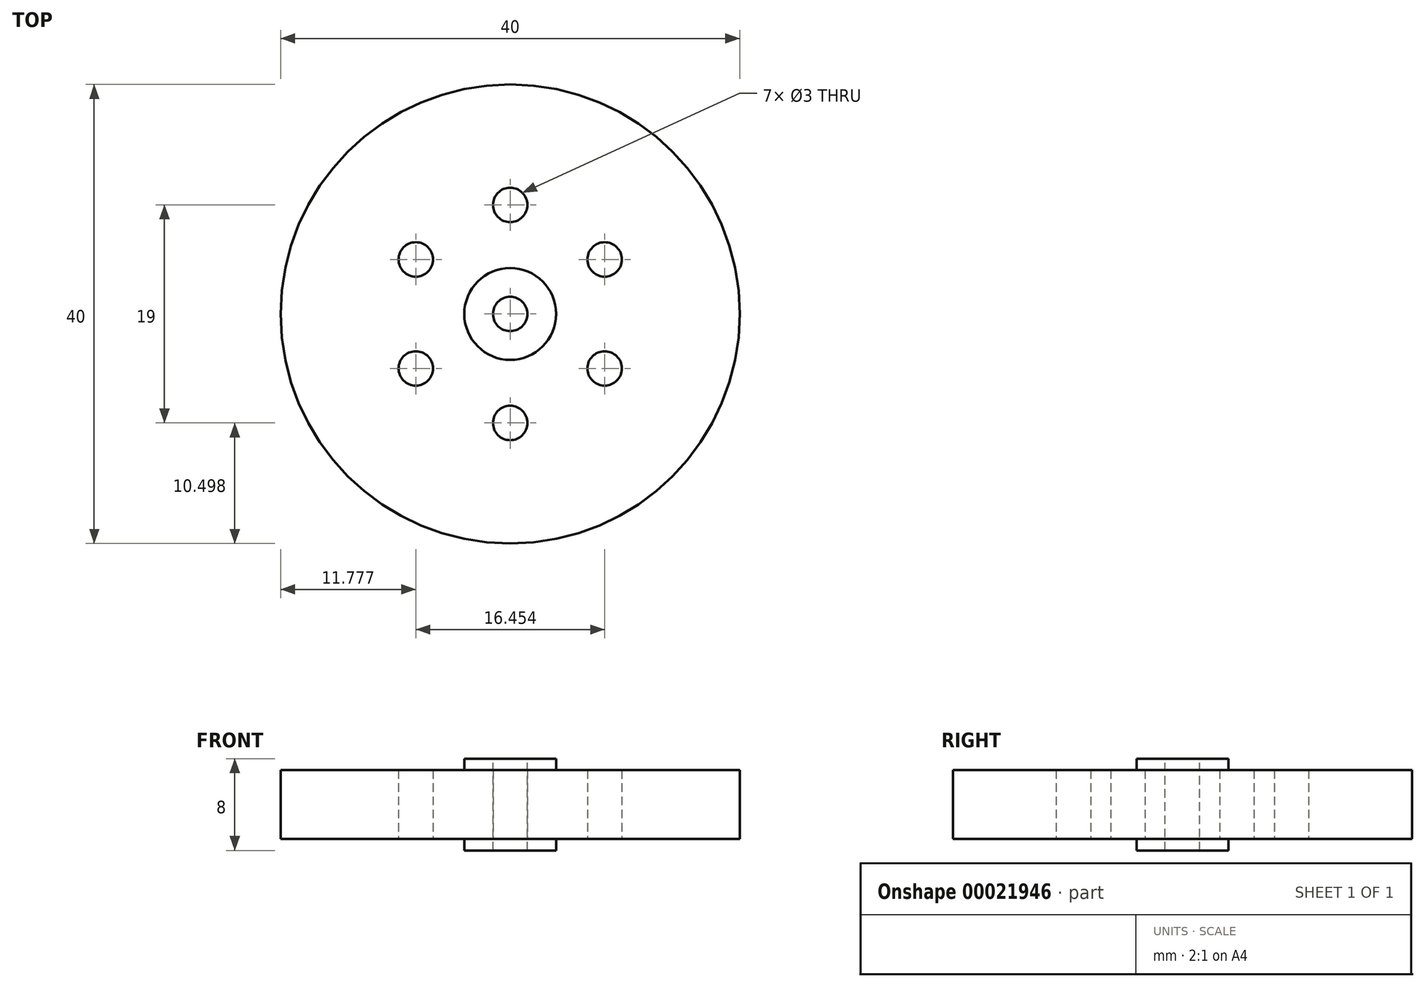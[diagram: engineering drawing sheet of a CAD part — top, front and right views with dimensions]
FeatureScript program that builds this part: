
annotation { "Feature Type Name" : "Feature", "Feature Type Description" : "" }
export const myFeature = defineFeature(function(context is Context, id is Id, definition is map)
    precondition{}
    {
        {
            var Q0;
            Q0=qCreatedBy(makeId("Top.planeOp"),FACE);
            var sketch = newSketch(context, id + "F0", { "sketchPlane" : qUnion([Q0])});
            skCircle(sketch, "E0", {"center": v(-9.55, 3.79) * mm, "radius": 20 * mm});
            skCircle(sketch, "E1", {"center": v(-9.55, 13.29) * mm, "radius": 1.5 * mm});
            skCircle(sketch, "E2.1.0", {"center": v(-17.77, 8.54) * mm, "radius": 1.5 * mm});
            skCircle(sketch, "E2.2.0", {"center": v(-17.77, -0.96) * mm, "radius": 1.5 * mm});
            skCircle(sketch, "E2.3.0", {"center": v(-9.55, -5.71) * mm, "radius": 1.5 * mm});
            skCircle(sketch, "E2.4.0", {"center": v(-1.32, -0.96) * mm, "radius": 1.5 * mm});
            skCircle(sketch, "E2.5.0", {"center": v(-1.32, 8.54) * mm, "radius": 1.5 * mm});
            skSolve(sketch);
        }
        {
            var Q0;
            Q0=makeQuery(id+"F0.imprint","IMPRINT",FACE,{"disambiguationData":[TD([[makeQuery(id+"F0.imprint","IMPRINT",EDGE,{"derivedFrom":sQuery(id+"F0.wireOp",EDGE,"E0")}),1.0]])]});
            extrude(context, id + "F1", {"entities" : qUnion([Q0]), "depth" : 6 * mm});
        }
        {
            var Q0;
            Q0=makeQuery(id+"F1.opExtrude","CAP_FACE",FACE,{"disambiguationData":[OSD([sQuery(id+"F0.wireOp",EDGE,"E0"),sQuery(id+"F0.wireOp",EDGE,"E1"),sQuery(id+"F0.wireOp",EDGE,"E2.1.0"),sQuery(id+"F0.wireOp",EDGE,"E2.2.0"),sQuery(id+"F0.wireOp",EDGE,"E2.3.0"),sQuery(id+"F0.wireOp",EDGE,"E2.4.0"),sQuery(id+"F0.wireOp",EDGE,"E2.5.0")])],"isStart":false});
            var sketch = newSketch(context, id + "F2", { "sketchPlane" : qUnion([Q0])});
            skCircle(sketch, "E3", {"center": v(-9.55, 3.79) * mm, "radius": 4 * mm});
            skSolve(sketch);
        }
        {
            var Q0;
            Q0 = qSketchRegion(id + "F2", true);
            var Q1;
            Q1=makeQuery(id+"F2.imprint","IMPRINT",FACE,{"disambiguationData":[TD([[makeQuery(id+"F2.imprint","IMPRINT",EDGE,{"derivedFrom":sQuery(id+"F2.wireOp",EDGE,"E3")}),1.0]])]});
            extrude(context, id + "F3", {"entities" : qUnion([Q0, Q1]), "operationType" : NewBodyOperationType.ADD, "depth" : 1 * mm});
        }
        {
            var Q0;
            Q0=makeQuery(id+"F3.opExtrude","CAP_FACE",FACE,{"disambiguationData":[OSD([sQuery(id+"F2.wireOp",EDGE,"E3")])],"isStart":false});
            var sketch = newSketch(context, id + "F4", { "sketchPlane" : qUnion([Q0])});
            skCircle(sketch, "E4", {"center": v(-9.55, 3.79) * mm, "radius": 1.5 * mm});
            skSolve(sketch);
        }
        {
            var Q0;
            Q0=makeQuery(id+"F4.imprint","IMPRINT",FACE,{"disambiguationData":[TD([[makeQuery(id+"F4.imprint","IMPRINT",EDGE,{"derivedFrom":sQuery(id+"F4.wireOp",EDGE,"E4")}),1.0]])]});
            extrude(context, id + "F5", {"entities" : qUnion([Q0]), "operationType" : NewBodyOperationType.REMOVE, "oppositeDirection" : true, "depth" : 25 * mm});
        }
        {
            var Q0;
            Q0=makeQuery(id+"F1.opExtrude","CAP_FACE",FACE,{"disambiguationData":[OSD([sQuery(id+"F0.wireOp",EDGE,"E0"),sQuery(id+"F0.wireOp",EDGE,"E1"),sQuery(id+"F0.wireOp",EDGE,"E2.1.0"),sQuery(id+"F0.wireOp",EDGE,"E2.2.0"),sQuery(id+"F0.wireOp",EDGE,"E2.3.0"),sQuery(id+"F0.wireOp",EDGE,"E2.4.0"),sQuery(id+"F0.wireOp",EDGE,"E2.5.0")])],"isStart":true});
            var sketch = newSketch(context, id + "F6", { "sketchPlane" : qUnion([Q0])});
            skCircle(sketch, "E5", {"center": v(-9.55, -3.79) * mm, "radius": 4 * mm});
            skSolve(sketch);
        }
        {
            var Q0;
            Q0=makeQuery(id+"F6.imprint","IMPRINT",FACE,{"disambiguationData":[TD([[makeQuery(id+"F6.imprint","IMPRINT",EDGE,{"derivedFrom":sQuery(id+"F6.wireOp",EDGE,"E5")}),1.0]])]});
            extrude(context, id + "F7", {"entities" : qUnion([Q0]), "operationType" : NewBodyOperationType.ADD, "depth" : 1 * mm});
        }
    });
